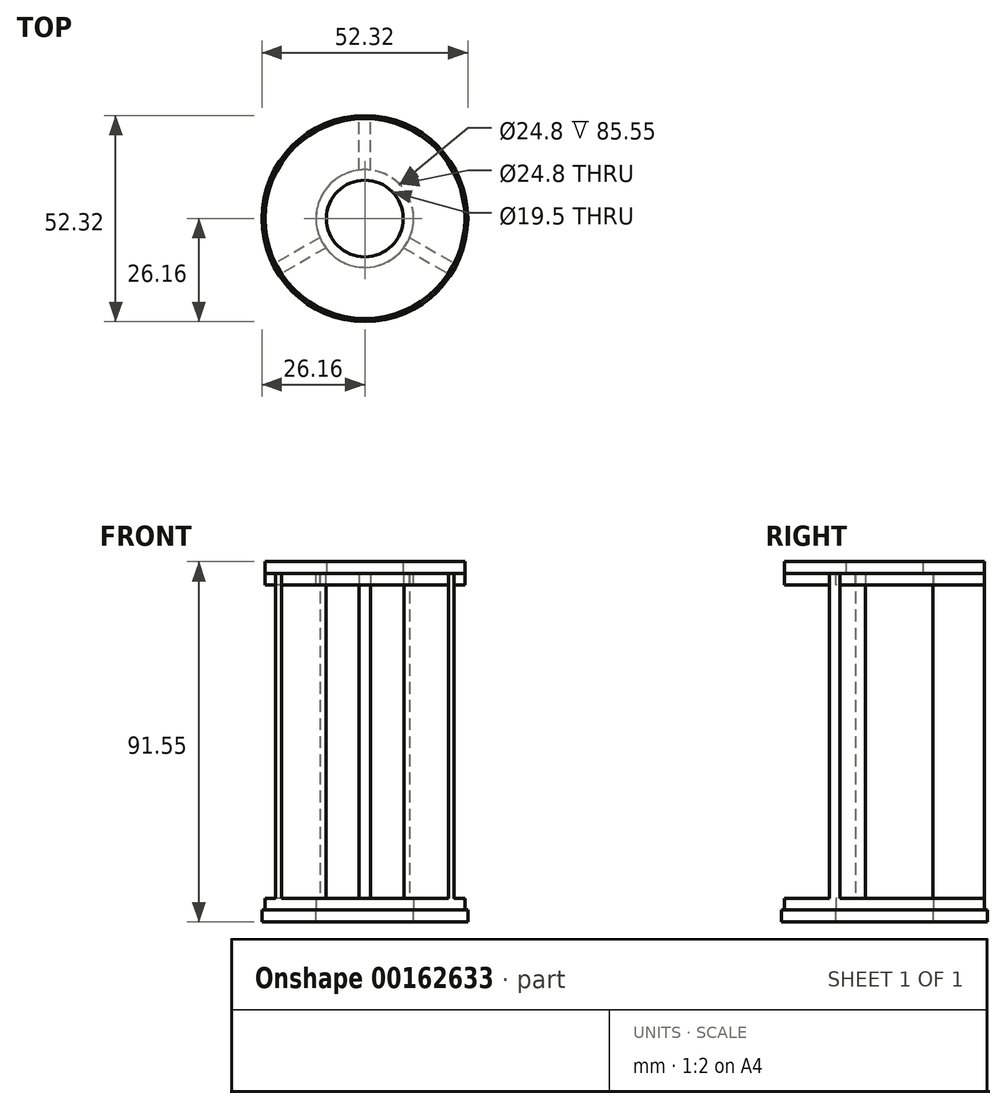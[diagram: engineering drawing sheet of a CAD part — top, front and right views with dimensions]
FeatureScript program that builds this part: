
annotation { "Feature Type Name" : "Feature", "Feature Type Description" : "" }
export const myFeature = defineFeature(function(context is Context, id is Id, definition is map)
    precondition{}
    {
        {
            var Q0;
            Q0=qCreatedBy(makeId("Top.planeOp"),FACE);
            var sketch = newSketch(context, id + "F0", { "sketchPlane" : qUnion([Q0])});
            skCircle(sketch, "E0", {"center": v(0, 0) * mm, "radius": 12.4 * mm});
            skCircle(sketch, "E1", {"center": v(0, 0) * mm, "radius": 26.16 * mm});
            skCircle(sketch, "E2", {"center": v(0, 0) * mm, "radius": 25.4 * mm});
            skSolve(sketch);
        }
        {
            var Q0;
            Q0 = qSketchRegion(id + "F0", true);
            var Q1;
            Q1=makeQuery(id+"F0.imprint","IMPRINT",FACE,{"disambiguationData":[TD([[makeQuery(id+"F0.imprint","IMPRINT",EDGE,{"derivedFrom":sQuery(id+"F0.wireOp",EDGE,"E0")}),-1.0]])]});
            extrude(context, id + "F1", {"entities" : qUnion([Q0, Q1]), "oppositeDirection" : true, "depth" : 3 * mm});
        }
        {
            var Q0;
            Q0=makeQuery(id+"F0.imprint","IMPRINT",FACE,{"disambiguationData":[TD([[makeQuery(id+"F0.imprint","IMPRINT",EDGE,{"derivedFrom":sQuery(id+"F0.wireOp",EDGE,"E0")}),-1.0]])]});
            extrude(context, id + "F2", {"entities" : qUnion([Q0]), "depth" : 3 * mm});
        }
        {
            var Q0;
            Q0=makeQuery(id+"F2.opExtrude","CAP_FACE",FACE,{"disambiguationData":[OSD([sQuery(id+"F0.wireOp",EDGE,"E0"),sQuery(id+"F0.wireOp",EDGE,"E2")])],"isStart":false});
            var sketch = newSketch(context, id + "F3", { "sketchPlane" : qUnion([Q0])});
            skLineSegment(sketch, "E3", {"start": v(0, 12.4) * mm, "end": v(0, 25.4) * mm, "construction": true});
            skLineSegment(sketch, "E4", {"start": v(1.5, 12.3) * mm, "end": v(1.5, 25.36) * mm});
            skLineSegment(sketch, "E5.MirrorCS", {"start": v(-1.5, 12.3) * mm, "end": v(-1.5, 25.36) * mm});
            skLineSegment(sketch, "E6.1.0", {"start": v(-9.9, -7.45) * mm, "end": v(-21.2, -13.98) * mm});
            skLineSegment(sketch, "E6.1.1", {"start": v(-11.4, -4.86) * mm, "end": v(-22.7, -11.38) * mm});
            skLineSegment(sketch, "E6.2.0", {"start": v(11.4, -4.86) * mm, "end": v(22.7, -11.38) * mm});
            skLineSegment(sketch, "E6.2.1", {"start": v(9.9, -7.45) * mm, "end": v(21.2, -13.98) * mm});
            skSolve(sketch);
        }
        {
            var Q0;
            {var subQ0=sQuery(id+"F3.wireOp",EDGE,"E6.2.0");Q0=makeQuery(id+"F3.imprint","IMPRINT",FACE,{"disambiguationData":[TD([[makeQuery(id+"F3.imprint","IMPRINT",EDGE,{"derivedFrom":subQ0}),-1.0]])]});}
            var Q1;
            {var subQ0=sQuery(id+"F3.wireOp",EDGE,"E6.1.0");Q1=makeQuery(id+"F3.imprint","IMPRINT",FACE,{"disambiguationData":[TD([[makeQuery(id+"F3.imprint","IMPRINT",EDGE,{"derivedFrom":subQ0}),-1.0]])]});}
            var Q2;
            {var subQ0=sQuery(id+"F3.wireOp",EDGE,"E4");Q2=makeQuery(id+"F3.imprint","IMPRINT",FACE,{"disambiguationData":[TD([[makeQuery(id+"F3.imprint","IMPRINT",EDGE,{"derivedFrom":subQ0}),1.0]])]});}
            extrude(context, id + "F4", {"entities" : qUnion([Q0, Q1, Q2]), "operationType" : NewBodyOperationType.ADD, "depth" : 82.55 * mm});
        }
        {
            var Q0;
            Q0=makeQuery(id+"F4.opExtrude","CAP_FACE",FACE,{"disambiguationData":[OSD([sQuery(id+"F0.wireOp",EDGE,"E0"),sQuery(id+"F0.wireOp",EDGE,"E2"),sQuery(id+"F3.wireOp",EDGE,"E4"),sQuery(id+"F3.wireOp",EDGE,"E5.MirrorCS")])],"isStart":false});
            var sketch = newSketch(context, id + "F5", { "sketchPlane" : qUnion([Q0])});
            skCircle(sketch, "E7.0", {"center": v(0, 0) * mm, "radius": 25.4 * mm});
            skCircle(sketch, "E8", {"center": v(0, 0) * mm, "radius": 9.75 * mm});
            skCircle(sketch, "E9.0", {"center": v(0, 0) * mm, "radius": 12.4 * mm});
            skLineSegment(sketch, "E10.0", {"start": v(9.9, -7.45) * mm, "end": v(21.2, -13.98) * mm});
            skLineSegment(sketch, "E11.0", {"start": v(11.4, -4.86) * mm, "end": v(22.7, -11.38) * mm});
            skLineSegment(sketch, "E12.0", {"start": v(-9.9, -7.45) * mm, "end": v(-21.2, -13.98) * mm});
            skLineSegment(sketch, "E13.0", {"start": v(-11.4, -4.86) * mm, "end": v(-22.7, -11.38) * mm});
            skLineSegment(sketch, "E14.0", {"start": v(-1.5, 12.3) * mm, "end": v(-1.5, 25.36) * mm});
            skLineSegment(sketch, "E15.0", {"start": v(1.5, 12.3) * mm, "end": v(1.5, 25.36) * mm});
            skSolve(sketch);
        }
        {
            var Q0;
            Q0=makeQuery(id+"F5.imprint","IMPRINT",FACE,{"disambiguationData":[TD([[makeQuery(id+"F5.imprint","IMPRINT",EDGE,{"derivedFrom":sQuery(id+"F5.wireOp",EDGE,"E8")}),-1.0]])]});
            var Q1;
            {var subQ1=sQuery(id+"F3.wireOp",EDGE,"E4");var subQ2=makeQuery(id+"F4.opExtrude","CAP_EDGE",EDGE,{"disambiguationData":[OSD([subQ1])],"isStart":false});Q1=makeQuery(id+"F5.imprint","IMPRINT",FACE,{"disambiguationData":[TD([[makeQuery(id+"F5.imprint","IMPRINT",EDGE,{"derivedFrom":subQ2}),1.0]])]});}
            var Q2;
            {var subQ0=sQuery(id+"F5.wireOp",EDGE,"E10.0");Q2=makeQuery(id+"F5.imprint","IMPRINT",FACE,{"disambiguationData":[TD([[makeQuery(id+"F5.imprint","IMPRINT",EDGE,{"derivedFrom":subQ0}),-1.0]])]});}
            var Q3;
            {var subQ2=sQuery(id+"F5.wireOp",EDGE,"E11.0");Q3=makeQuery(id+"F5.imprint","IMPRINT",FACE,{"disambiguationData":[TD([[makeQuery(id+"F5.imprint","IMPRINT",EDGE,{"derivedFrom":subQ2}),1.0]])]});}
            var Q4;
            {var subQ0=sQuery(id+"F5.wireOp",EDGE,"E10.0");Q4=makeQuery(id+"F5.imprint","IMPRINT",FACE,{"disambiguationData":[TD([[makeQuery(id+"F5.imprint","IMPRINT",EDGE,{"derivedFrom":subQ0}),1.0]])]});}
            var Q5;
            {var subQ2=sQuery(id+"F5.wireOp",EDGE,"E13.0");Q5=makeQuery(id+"F5.imprint","IMPRINT",FACE,{"disambiguationData":[TD([[makeQuery(id+"F5.imprint","IMPRINT",EDGE,{"derivedFrom":subQ2}),-1.0]])]});}
            var Q6;
            {var subQ0=sQuery(id+"F5.wireOp",EDGE,"E12.0");Q6=makeQuery(id+"F5.imprint","IMPRINT",FACE,{"disambiguationData":[TD([[makeQuery(id+"F5.imprint","IMPRINT",EDGE,{"derivedFrom":subQ0}),-1.0]])]});}
            var Q7;
            {var subQ2=sQuery(id+"F5.wireOp",EDGE,"E14.0");Q7=makeQuery(id+"F5.imprint","IMPRINT",FACE,{"disambiguationData":[TD([[makeQuery(id+"F5.imprint","IMPRINT",EDGE,{"derivedFrom":subQ2}),-1.0]])]});}
            extrude(context, id + "F6", {"entities" : qUnion([Q0, Q1, Q2, Q3, Q4, Q5, Q6, Q7]), "depth" : 3 * mm});
        }
        {
            var Q0;
            {var subQ2=sQuery(id+"F5.wireOp",EDGE,"E11.0");Q0=makeQuery(id+"F5.imprint","IMPRINT",FACE,{"disambiguationData":[TD([[makeQuery(id+"F5.imprint","IMPRINT",EDGE,{"derivedFrom":subQ2}),1.0]])]});}
            var Q1;
            {var subQ2=sQuery(id+"F5.wireOp",EDGE,"E13.0");Q1=makeQuery(id+"F5.imprint","IMPRINT",FACE,{"disambiguationData":[TD([[makeQuery(id+"F5.imprint","IMPRINT",EDGE,{"derivedFrom":subQ2}),-1.0]])]});}
            var Q2;
            {var subQ0=sQuery(id+"F5.wireOp",EDGE,"E10.0");Q2=makeQuery(id+"F5.imprint","IMPRINT",FACE,{"disambiguationData":[TD([[makeQuery(id+"F5.imprint","IMPRINT",EDGE,{"derivedFrom":subQ0}),-1.0]])]});}
            extrude(context, id + "F7", {"entities" : qUnion([Q0, Q1, Q2]), "oppositeDirection" : true, "depth" : 3 * mm});
        }
    });
